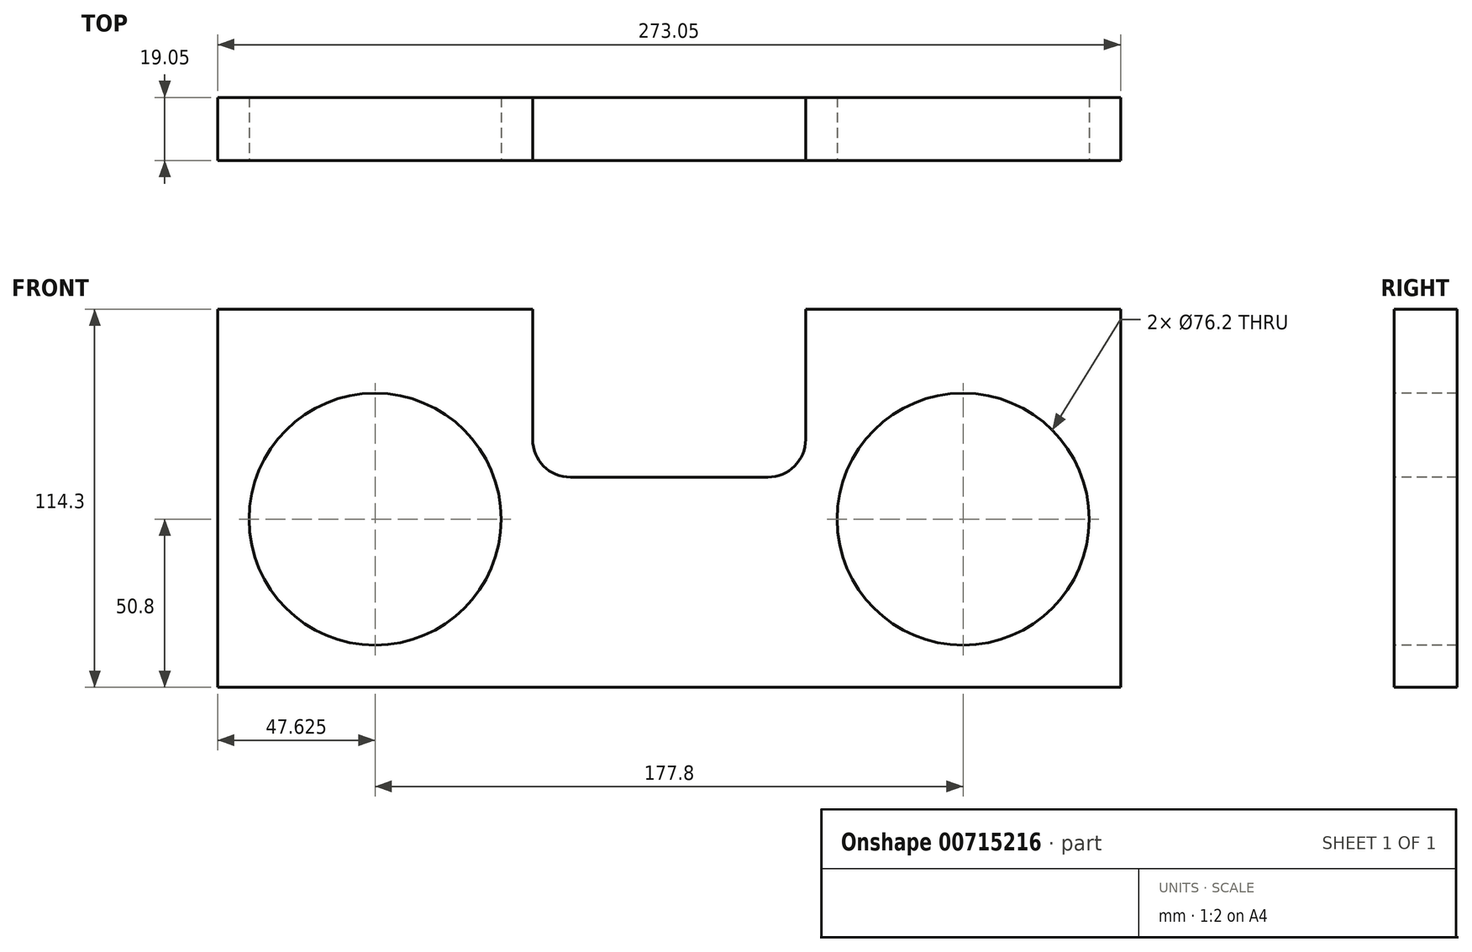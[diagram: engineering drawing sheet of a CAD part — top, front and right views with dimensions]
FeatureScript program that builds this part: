
annotation { "Feature Type Name" : "Feature", "Feature Type Description" : "" }
export const myFeature = defineFeature(function(context is Context, id is Id, definition is map)
    precondition{}
    {
        {
            var Q0;
            Q0=qCreatedBy(makeId("Front.planeOp"),FACE);
            var sketch = newSketch(context, id + "F0", { "sketchPlane" : qUnion([Q0])});
            skLineSegment(sketch, "E0.bottom", {"start": v(0, 0) * mm, "end": v(273.05, 0) * mm});
            skLineSegment(sketch, "E0.top", {"start": v(0, 114.3) * mm, "end": v(273.05, 114.3) * mm});
            skLineSegment(sketch, "E0.left", {"start": v(0, 0) * mm, "end": v(0, 114.3) * mm});
            skLineSegment(sketch, "E0.right", {"start": v(273.05, 0) * mm, "end": v(273.05, 114.3) * mm});
            skSolve(sketch);
        }
        {
            var Q0;
            Q0=qSketchRegion(id+"F0",true);
            extrude(context, id + "F1", {"entities" : qUnion([Q0]), "depth" : 19.05 * mm, "offsetDistance" : 25.4 * mm});
        }
        {
            var Q0;
            Q0=makeQuery(id+"F1.opExtrude","CAP_FACE",FACE,{"disambiguationData":[OSD([sQuery(id+"F0.wireOp",EDGE,"E0.bottom"),sQuery(id+"F0.wireOp",EDGE,"E0.top"),sQuery(id+"F0.wireOp",EDGE,"E0.left"),sQuery(id+"F0.wireOp",EDGE,"E0.right")])],"isStart":false});
            var sketch = newSketch(context, id + "F2", { "sketchPlane" : qUnion([Q0])});
            skCircle(sketch, "E1", {"center": v(47.63, 50.8) * mm, "radius": 38.1 * mm});
            skCircle(sketch, "E2", {"center": v(225.43, 50.8) * mm, "radius": 38.1 * mm});
            skSolve(sketch);
        }
        {
            var Q0;
            Q0=qSketchRegion(id+"F2",true);
            extrude(context, id + "F3", {"entities" : qUnion([Q0]), "operationType" : NewBodyOperationType.REMOVE, "oppositeDirection" : true, "depth" : 25.4 * mm, "offsetDistance" : 25.4 * mm});
        }
        {
            var Q0;
            Q0=makeQuery(id+"F1.opExtrude","CAP_FACE",FACE,{"disambiguationData":[OSD([sQuery(id+"F0.wireOp",EDGE,"E0.bottom"),sQuery(id+"F0.wireOp",EDGE,"E0.top"),sQuery(id+"F0.wireOp",EDGE,"E0.left"),sQuery(id+"F0.wireOp",EDGE,"E0.right")])],"isStart":false});
            var sketch = newSketch(context, id + "F4", { "sketchPlane" : qUnion([Q0])});
            skLineSegment(sketch, "E3", {"start": v(95.25, 114.3) * mm, "end": v(95.25, 74.93) * mm});
            skLineSegment(sketch, "E4", {"start": v(106.68, 63.5) * mm, "end": v(166.37, 63.5) * mm});
            skLineSegment(sketch, "E5", {"start": v(177.8, 74.93) * mm, "end": v(177.8, 114.3) * mm});
            skPoint(sketch, "E6.visualSharp", {"position": v(95.25, 63.5) * mm});
            skArc(sketch, "E6.filletArc", {"start": v(95.25, 74.93) * mm, "mid": v(98.6, 66.85) * mm, "end": v(106.68, 63.5) * mm});
            skPoint(sketch, "E7.visualSharp", {"position": v(177.8, 63.5) * mm});
            skArc(sketch, "E7.filletArc", {"start": v(166.37, 63.5) * mm, "mid": v(174.45, 66.85) * mm, "end": v(177.8, 74.93) * mm});
            skSolve(sketch);
        }
        {
            var Q0;
            Q0=qSketchRegion(id+"F4",true);
            var Q1;
            {var subQ1=sQuery(id+"F4.wireOp",EDGE,"E3");Q1=makeQuery(id+"F4.imprint","IMPRINT",FACE,{"disambiguationData":[TD([[makeQuery(id+"F4.imprint","IMPRINT",EDGE,{"derivedFrom":subQ1}),1.0]])]});}
            extrude(context, id + "F5", {"entities" : qUnion([Q0, Q1]), "operationType" : NewBodyOperationType.REMOVE, "oppositeDirection" : true, "depth" : 25.4 * mm, "offsetDistance" : 25.4 * mm});
        }
    });
